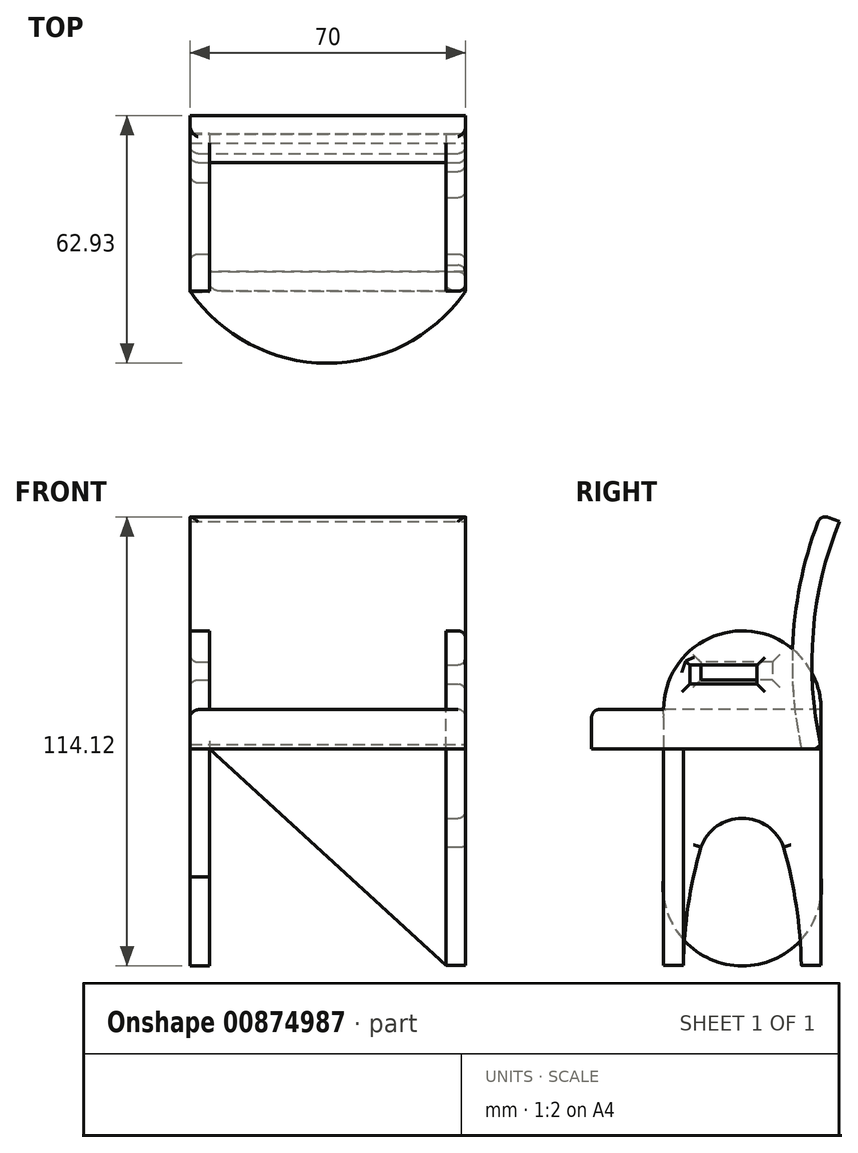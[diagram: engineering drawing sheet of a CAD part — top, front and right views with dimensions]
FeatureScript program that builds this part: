
annotation { "Feature Type Name" : "Feature", "Feature Type Description" : "" }
export const myFeature = defineFeature(function(context is Context, id is Id, definition is map)
    precondition{}
    {
        {
            var Q0;
            Q0=qCreatedBy(makeId("Top.planeOp"),FACE);
            var sketch = newSketch(context, id + "F0", { "sketchPlane" : qUnion([Q0])});
            skLineSegment(sketch, "E0.bottom", {"start": v(-70, 0) * mm, "end": v(0, 0) * mm});
            skLineSegment(sketch, "E0.top", {"start": v(-81.65, -40) * mm, "end": v(-70, -40) * mm});
            skLineSegment(sketch, "E0.left", {"start": v(-70, 0) * mm, "end": v(-70, -40) * mm});
            skLineSegment(sketch, "E0.right", {"start": v(0, 0) * mm, "end": v(0, -40) * mm});
            skLineSegment(sketch, "E1.trimOffspring", {"start": v(-0.2, -40) * mm, "end": v(0, -40) * mm});
            skPoint(sketch, "E2.center.orphan", {"position": v(-35, -40) * mm});
            skLineSegment(sketch, "E3", {"start": v(-81.65, -40) * mm, "end": v(0, -40) * mm, "construction": true});
            skArc(sketch, "E4", {"start": v(-70, -40) * mm, "mid": v(-35, -58.29) * mm, "end": v(0, -40) * mm});
            skSolve(sketch);
        }
        {
            var Q0;
            Q0 = qSketchRegion(id + "F0", true);
            extrude(context, id + "F1", {"entities" : qUnion([Q0]), "depth" : 10 * mm, "offsetDistance" : 25 * mm});
        }
        {
            var Q0;
            Q0=qCreatedBy(makeId("Right.planeOp"),FACE);
            var sketch = newSketch(context, id + "F2", { "sketchPlane" : qUnion([Q0])});
            skLineSegment(sketch, "E5.left", {"start": v(0, 0) * mm, "end": v(0, -55) * mm});
            skLineSegment(sketch, "E5.right", {"start": v(-40, 0) * mm, "end": v(-40, -55) * mm});
            skPoint(sketch, "E6.start.orphan", {"position": v(-20, 0) * mm});
            skLineSegment(sketch, "E7", {"start": v(-40, -55) * mm, "end": v(-35, -55) * mm});
            skLineSegment(sketch, "E8", {"start": v(0, -55) * mm, "end": v(-5, -55) * mm});
            skArc(sketch, "E9", {"start": v(-30.52, -24.97) * mm, "mid": v(-33.76, -39.84) * mm, "end": v(-35, -55) * mm});
            skArc(sketch, "E10", {"start": v(-5, -55) * mm, "mid": v(-6.28, -39.84) * mm, "end": v(-9.53, -24.97) * mm});
            skArc(sketch, "E11", {"start": v(-9.08, -26.57) * mm, "mid": v(-20.02, -17.6) * mm, "end": v(-30.97, -26.57) * mm});
            skPoint(sketch, "E11.endSnap0", {"position": v(-9.08, -26.57) * mm});
            skLineSegment(sketch, "E12.left", {"start": v(-40, 0) * mm, "end": v(-40, 10) * mm});
            skLineSegment(sketch, "E12.right", {"start": v(0, 0) * mm, "end": v(0, 10) * mm});
            skArc(sketch, "E13", {"start": v(0, 10) * mm, "mid": v(-20, 30) * mm, "end": v(-40, 10) * mm});
            skLineSegment(sketch, "E14.bottom", {"start": v(-33.36, 21.28) * mm, "end": v(-16.24, 21.28) * mm});
            skLineSegment(sketch, "E14.top", {"start": v(-33.36, 16.44) * mm, "end": v(-16.24, 16.44) * mm});
            skLineSegment(sketch, "E14.left", {"start": v(-33.36, 21.28) * mm, "end": v(-33.36, 16.44) * mm});
            skLineSegment(sketch, "E14.right", {"start": v(-16.24, 21.28) * mm, "end": v(-16.24, 16.44) * mm});
            skSolve(sketch);
        }
        {
            var Q0;
            Q0 = qSketchRegion(id + "F2", true);
            extrude(context, id + "F3", {"entities" : qUnion([Q0]), "oppositeDirection" : true, "depth" : 5 * mm, "offsetDistance" : 25 * mm});
        }
        {
            var Q0;
            Q0=makeQuery(id+"F3.opExtrude","CAP_FACE",FACE,{"disambiguationData":[OSD([sQuery(id+"F2.wireOp",EDGE,"E5.bottom"),sQuery(id+"F2.wireOp",EDGE,"E5.left"),sQuery(id+"F2.wireOp",EDGE,"E5.right"),sQuery(id+"F2.wireOp",EDGE,"E7"),sQuery(id+"F2.wireOp",EDGE,"E8"),sQuery(id+"F2.wireOp",EDGE,"E9"),sQuery(id+"F2.wireOp",EDGE,"E10"),sQuery(id+"F2.wireOp",EDGE,"E11")])],"isStart":false});
            var sketch = newSketch(context, id + "F4", { "sketchPlane" : qUnion([Q0])});
            skPoint(sketch, "E15.center.orphan", {"position": v(20, 0) * mm});
            skLineSegment(sketch, "E16.bottom", {"start": v(12.4, 22.02) * mm, "end": v(30.52, 22.02) * mm});
            skLineSegment(sketch, "E16.top", {"start": v(12.4, 17.56) * mm, "end": v(30.52, 17.56) * mm});
            skLineSegment(sketch, "E16.left", {"start": v(12.4, 22.02) * mm, "end": v(12.4, 17.56) * mm});
            skLineSegment(sketch, "E16.right", {"start": v(30.52, 22.02) * mm, "end": v(30.52, 17.56) * mm});
            skPoint(sketch, "E17.trimOffspring.end.orphan", {"position": v(40, -35) * mm});
            skPoint(sketch, "E18.center.orphan", {"position": v(20, -44.6) * mm});
            skPoint(sketch, "E19.start.orphan", {"position": v(40, -44.6) * mm});
            skPoint(sketch, "E20.center.orphan", {"position": v(21.44, -27.56) * mm});
            skPoint(sketch, "E20.start.orphan", {"position": v(2.87, -20.12) * mm});
            skPoint(sketch, "E21.end.orphan", {"position": v(0, -44.6) * mm});
            skLineSegment(sketch, "E22.top", {"start": v(17.58, -55) * mm, "end": v(22.42, -55) * mm});
            skLineSegment(sketch, "E22.left", {"start": v(0, 10) * mm, "end": v(0, -37.42) * mm});
            skLineSegment(sketch, "E22.right", {"start": v(40, 10) * mm, "end": v(40, -37.42) * mm});
            skArc(sketch, "E23", {"start": v(40, 10) * mm, "mid": v(20, 30) * mm, "end": v(0, 10) * mm});
            skArc(sketch, "E24", {"start": v(0, -32.58) * mm, "mid": v(20, -55.15) * mm, "end": v(40, -32.58) * mm});
            skSolve(sketch);
        }
        {
            var Q0;
            Q0 = qSketchRegion(id + "F4", true);
            extrude(context, id + "F5", {"entities" : qUnion([Q0]), "operationType" : NewBodyOperationType.ADD, "depth" : 65 * mm, "offsetDistance" : 25 * mm, "hasSecondDirection" : true, "secondDirectionOppositeDirection" : false, "secondDirectionDepth" : 60 * mm});
        }
        {
            var Q0;
            Q0=qCreatedBy(makeId("Front.planeOp"),FACE);
            var sketch = newSketch(context, id + "F6", { "sketchPlane" : qUnion([Q0])});
            skLineSegment(sketch, "E25.bottom", {"start": v(0, 0) * mm, "end": v(-65, 0) * mm});
            skLineSegment(sketch, "E25.top", {"start": v(0, -55) * mm, "end": v(-5, -55) * mm});
            skLineSegment(sketch, "E25.left", {"start": v(0, 0) * mm, "end": v(0, -55) * mm});
            skLineSegment(sketch, "E25.right", {"start": v(-65, 0) * mm, "end": v(-65, -55) * mm});
            skLineSegment(sketch, "E26", {"start": v(-65, 0) * mm, "end": v(-5, -55) * mm});
            skSolve(sketch);
        }
        {
            var Q0;
            Q0 = qSketchRegion(id + "F6", true);
            extrude(context, id + "F7", {"entities" : qUnion([Q0]), "depth" : 40 * mm, "offsetDistance" : 25 * mm, "hasSecondDirection" : true, "secondDirectionOppositeDirection" : false, "secondDirectionDepth" : 35 * mm});
        }
        {
            var Q0;
            Q0=qCreatedBy(makeId("Right.planeOp"),FACE);
            var sketch = newSketch(context, id + "F8", { "sketchPlane" : qUnion([Q0])});
            skLineSegment(sketch, "E27.bottom", {"start": v(0, 0) * mm, "end": v(-5, 0) * mm});
            skArc(sketch, "E28", {"start": v(0, 59.58) * mm, "mid": v(-6.98, 30.16) * mm, "end": v(-5, 0) * mm});
            skArc(sketch, "E29.0", {"start": v(4.64, 57.71) * mm, "mid": v(-2, 29.75) * mm, "end": v(-0.11, 1.06) * mm});
            skLineSegment(sketch, "E30", {"start": v(0, 59.58) * mm, "end": v(4.64, 57.71) * mm});
            skLineSegment(sketch, "E31", {"start": v(-0.11, 1.06) * mm, "end": v(0, 0) * mm});
            skSolve(sketch);
        }
        {
            var Q0;
            Q0 = qSketchRegion(id + "F8", true);
            extrude(context, id + "F9", {"entities" : qUnion([Q0]), "oppositeDirection" : true, "depth" : 70 * mm, "offsetDistance" : 25 * mm});
        }
        {
            var Q0;
            Q0=makeQuery(id+"F9.opExtrude","SWEPT_EDGE",EDGE,{"disambiguationData":[OSD([sQuery(id+"F8.wireOp",EDGE,"E28"),sQuery(id+"F8.wireOp",EDGE,"E30")])]});
            var Q1;
            Q1=makeQuery(id+"F9.opExtrude","CAP_EDGE",EDGE,{"disambiguationData":[OSD([sQuery(id+"F8.wireOp",EDGE,"E28")])],"isStart":true});
            var Q2;
            Q2=makeQuery(id+"F9.opExtrude","CAP_EDGE",EDGE,{"disambiguationData":[OSD([sQuery(id+"F8.wireOp",EDGE,"E28")])],"isStart":false});
            var Q3;
            Q3=makeQuery(id+"F3.opExtrude","CAP_EDGE",EDGE,{"disambiguationData":[OSD([sQuery(id+"F2.wireOp",EDGE,"E5.left")])],"isStart":true});
            var Q4;
            Q4=makeQuery(id+"F7.opExtrude","CAP_EDGE",EDGE,{"disambiguationData":[OSD([sQuery(id+"F6.wireOp",EDGE,"E26")])],"isStart":false});
            var Q5;
            Q5=makeQuery(id+"F1.opExtrude","CAP_EDGE",EDGE,{"disambiguationData":[OSD([sQuery(id+"F0.wireOp",EDGE,"E4")])],"isStart":false});
            var Q6;
            Q6=makeQuery(id+"F1.opExtrude","CAP_EDGE",EDGE,{"disambiguationData":[OSD([sQuery(id+"F0.wireOp",EDGE,"E0.right")])],"isStart":false});
            var Q7;
            Q7=makeQuery(id+"F1.opExtrude","SWEPT_EDGE",EDGE,{"disambiguationData":[OSD([sQuery(id+"F0.wireOp",EDGE,"E0.right"),sQuery(id+"F0.wireOp",EDGE,"E4")])]});
            var Q8;
            Q8=makeQuery(id+"F3.opExtrude","CAP_EDGE",EDGE,{"disambiguationData":[OSD([sQuery(id+"F2.wireOp",EDGE,"E11")])],"isStart":true});
            var Q9;
            Q9=makeQuery(id+"F3.opExtrude","CAP_EDGE",EDGE,{"disambiguationData":[OSD([sQuery(id+"F2.wireOp",EDGE,"E10")])],"isStart":true});
            var Q10;
            Q10=makeQuery(id+"F3.opExtrude","CAP_EDGE",EDGE,{"disambiguationData":[OSD([sQuery(id+"F2.wireOp",EDGE,"E9")])],"isStart":true});
            var Q11;
            Q11=makeQuery(id+"F1.opExtrude","CAP_EDGE",EDGE,{"disambiguationData":[OSD([sQuery(id+"F0.wireOp",EDGE,"E0.bottom")])],"isStart":true});
            var Q12;
            Q12=makeQuery(id+"F3.opExtrude","CAP_EDGE",EDGE,{"disambiguationData":[OSD([sQuery(id+"F2.wireOp",EDGE,"E5.right")])],"isStart":true});
            var Q13;
            Q13=makeQuery(id+"F5.opExtrude","CAP_EDGE",EDGE,{"disambiguationData":[OSD([sQuery(id+"F4.wireOp",EDGE,"E16.bottom")])],"isStart":false});
            var Q14;
            Q14=makeQuery(id+"F5.opExtrude","CAP_EDGE",EDGE,{"disambiguationData":[OSD([sQuery(id+"F4.wireOp",EDGE,"E16.left")])],"isStart":false});
            var Q15;
            Q15=makeQuery(id+"F5.opExtrude","CAP_EDGE",EDGE,{"disambiguationData":[OSD([sQuery(id+"F4.wireOp",EDGE,"E16.top")])],"isStart":false});
            var Q16;
            Q16=makeQuery(id+"F5.opExtrude","CAP_EDGE",EDGE,{"disambiguationData":[OSD([sQuery(id+"F4.wireOp",EDGE,"E16.right")])],"isStart":false});
            var Q17;
            Q17=makeQuery(id+"F3.opExtrude","CAP_EDGE",EDGE,{"disambiguationData":[OSD([sQuery(id+"F2.wireOp",EDGE,"E14.top")])],"isStart":true});
            var Q18;
            Q18=makeQuery(id+"F3.opExtrude","CAP_EDGE",EDGE,{"disambiguationData":[OSD([sQuery(id+"F2.wireOp",EDGE,"E14.right")])],"isStart":true});
            var Q19;
            Q19=makeQuery(id+"F3.opExtrude","CAP_EDGE",EDGE,{"disambiguationData":[OSD([sQuery(id+"F2.wireOp",EDGE,"E14.left")])],"isStart":true});
            var Q20;
            Q20=makeQuery(id+"F3.opExtrude","CAP_EDGE",EDGE,{"disambiguationData":[OSD([sQuery(id+"F2.wireOp",EDGE,"E14.bottom")])],"isStart":true});
            fillet(context, id + "F10", {"entities" : qUnion([Q0, Q1, Q2, Q3, Q4, Q5, Q6, Q7, Q8, Q9, Q10, Q11, Q12, Q13, Q14, Q15, Q16, Q17, Q18, Q19, Q20]), "radius" : 2 * mm, "tangentPropagation" : true, "allowEdgeOverflow" : false});
        }
    });
